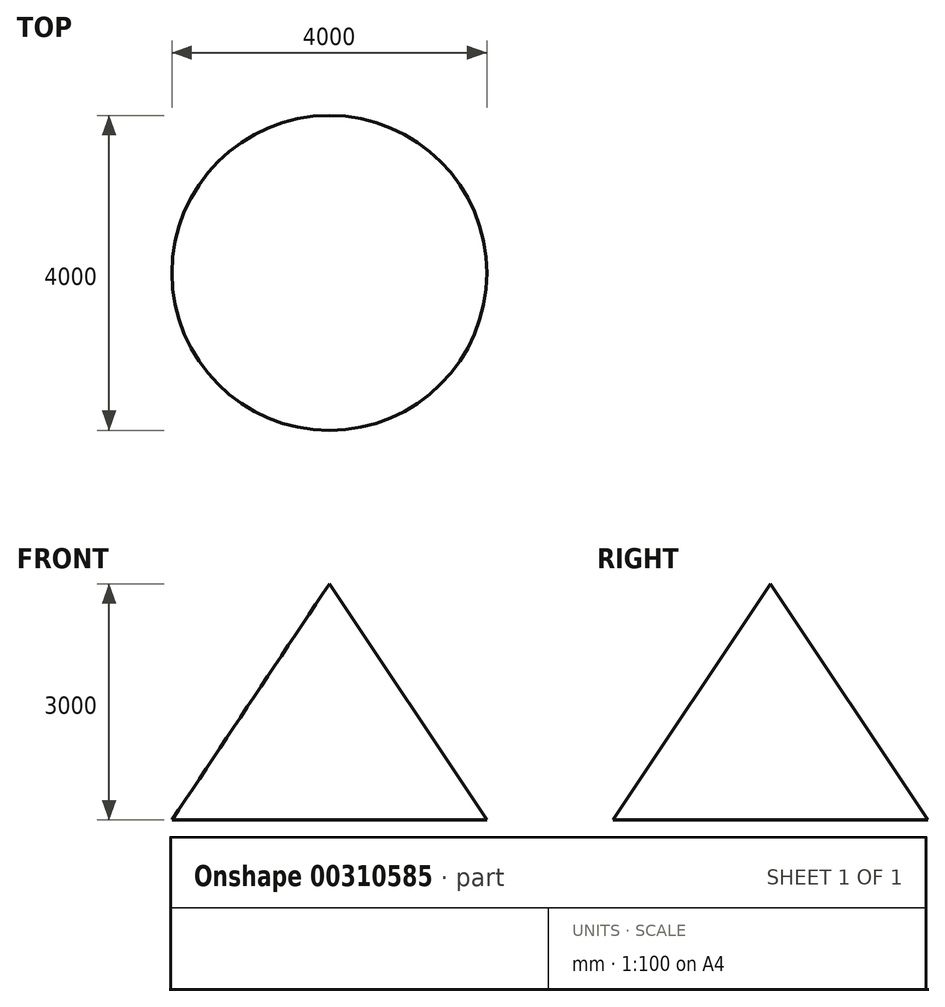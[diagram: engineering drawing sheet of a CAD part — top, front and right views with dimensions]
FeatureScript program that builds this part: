
annotation { "Feature Type Name" : "Feature", "Feature Type Description" : "" }
export const myFeature = defineFeature(function(context is Context, id is Id, definition is map)
    precondition{}
    {
        {
            var Q0;
            Q0=qCreatedBy(makeId("Front.planeOp"),FACE);
            var sketch = newSketch(context, id + "F0", { "sketchPlane" : qUnion([Q0])});
            skLineSegment(sketch, "E0", {"start": v(0, 1681.45) * mm, "end": v(0, -1318.55) * mm});
            skLineSegment(sketch, "E1", {"start": v(0, -1318.55) * mm, "end": v(-2000, -1318.55) * mm});
            skLineSegment(sketch, "E2", {"start": v(0, -1318.55) * mm, "end": v(2000, -1318.55) * mm});
            skLineSegment(sketch, "E3", {"start": v(0, 1681.45) * mm, "end": v(-2000, -1318.55) * mm});
            skLineSegment(sketch, "E4", {"start": v(0, 1681.45) * mm, "end": v(2000, -1318.55) * mm});
            skSolve(sketch);
        }
        {
            var Q0;
            Q0=makeQuery(id+"F0.imprint","IMPRINT",FACE,{"disambiguationData":[TD([[makeQuery(id+"F0.imprint","IMPRINT",EDGE,{"derivedFrom":sQuery(id+"F0.wireOp",EDGE,"E0")}),-1.0]])]});
            var Q1;
            Q1=sQuery(id+"F0.wireOp",EDGE,"E0");
            revolve(context, id + "F1", {"entities" : qUnion([Q0]), "axis" : qUnion([Q1]), "revolveType" : RevolveType.FULL});
        }
    });
